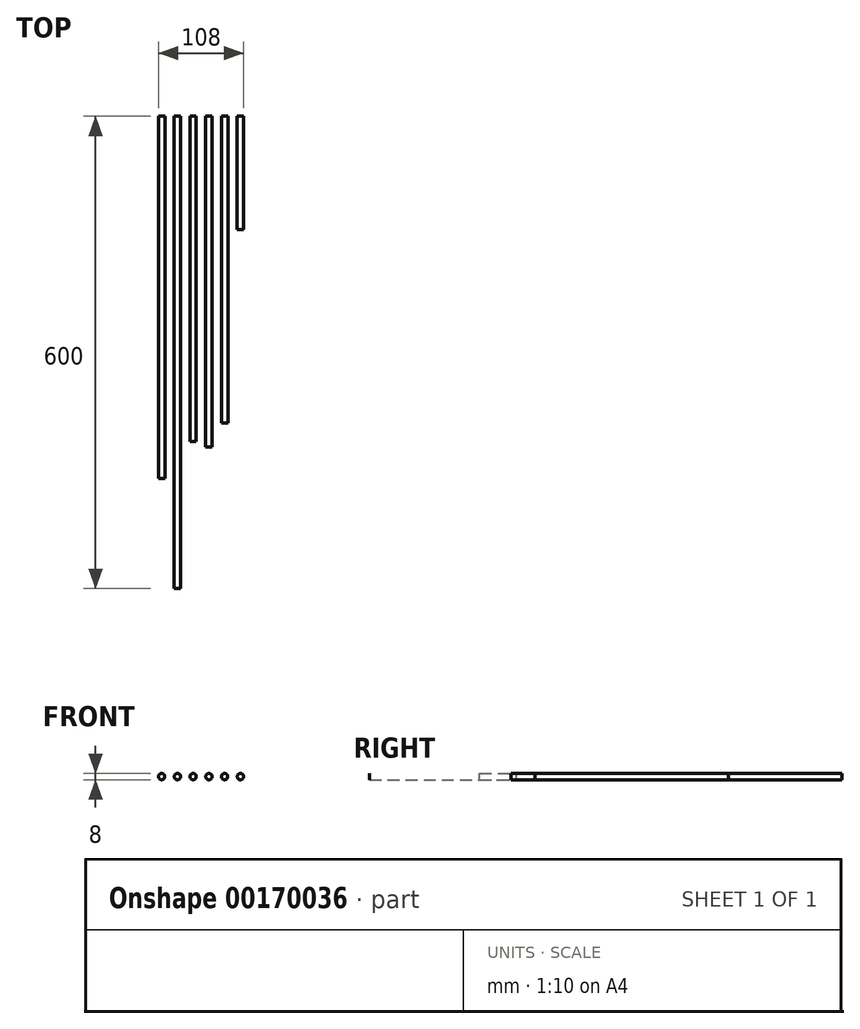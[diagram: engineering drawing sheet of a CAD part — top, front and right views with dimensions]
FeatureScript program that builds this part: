
annotation { "Feature Type Name" : "Feature", "Feature Type Description" : "" }
export const myFeature = defineFeature(function(context is Context, id is Id, definition is map)
    precondition{}
    {
        {
            var Q0;
            Q0=qCreatedBy(makeId("Front.planeOp"),FACE);
            var sketch = newSketch(context, id + "F0", { "sketchPlane" : qUnion([Q0])});
            skCircle(sketch, "E0", {"center": v(0, 0) * mm, "radius": 4 * mm});
            skCircle(sketch, "E1", {"center": v(20, 0) * mm, "radius": 4 * mm});
            skCircle(sketch, "E2", {"center": v(-20, 0) * mm, "radius": 4 * mm});
            skCircle(sketch, "E3", {"center": v(-40, 0) * mm, "radius": 4 * mm});
            skCircle(sketch, "E4", {"center": v(-60, 0) * mm, "radius": 4 * mm});
            skCircle(sketch, "E5", {"center": v(40, 0) * mm, "radius": 4 * mm});
            skSolve(sketch);
        }
        {
            var Q0;
            Q0=makeQuery(id+"F0.imprint","IMPRINT",FACE,{"disambiguationData":[TD([[makeQuery(id+"F0.imprint","IMPRINT",EDGE,{"derivedFrom":sQuery(id+"F0.wireOp",EDGE,"E0")}),1.0]])]});
            extrude(context, id + "F1", {"entities" : qUnion([Q0]), "depth" : 420 * mm});
        }
        {
            var Q0;
            Q0=makeQuery(id+"F0.imprint","IMPRINT",FACE,{"disambiguationData":[TD([[makeQuery(id+"F0.imprint","IMPRINT",EDGE,{"derivedFrom":sQuery(id+"F0.wireOp",EDGE,"E1")}),1.0]])]});
            extrude(context, id + "F2", {"entities" : qUnion([Q0]), "depth" : 390 * mm});
        }
        {
            var Q0;
            Q0=makeQuery(id+"F0.imprint","IMPRINT",FACE,{"disambiguationData":[TD([[makeQuery(id+"F0.imprint","IMPRINT",EDGE,{"derivedFrom":sQuery(id+"F0.wireOp",EDGE,"E2")}),1.0]])]});
            extrude(context, id + "F3", {"entities" : qUnion([Q0]), "depth" : 413 * mm});
        }
        {
            var Q0;
            Q0=makeQuery(id+"F0.imprint","IMPRINT",FACE,{"disambiguationData":[TD([[makeQuery(id+"F0.imprint","IMPRINT",EDGE,{"derivedFrom":sQuery(id+"F0.wireOp",EDGE,"E3")}),1.0]])]});
            extrude(context, id + "F4", {"entities" : qUnion([Q0]), "depth" : 600 * mm});
        }
        {
            var Q0;
            Q0=makeQuery(id+"F0.imprint","IMPRINT",FACE,{"disambiguationData":[TD([[makeQuery(id+"F0.imprint","IMPRINT",EDGE,{"derivedFrom":sQuery(id+"F0.wireOp",EDGE,"E4")}),1.0]])]});
            extrude(context, id + "F5", {"entities" : qUnion([Q0]), "depth" : 460 * mm});
        }
        {
            var Q0;
            Q0=makeQuery(id+"F0.imprint","IMPRINT",FACE,{"disambiguationData":[TD([[makeQuery(id+"F0.imprint","IMPRINT",EDGE,{"derivedFrom":sQuery(id+"F0.wireOp",EDGE,"E5")}),1.0]])]});
            extrude(context, id + "F6", {"entities" : qUnion([Q0]), "depth" : 144 * mm});
        }
    });
